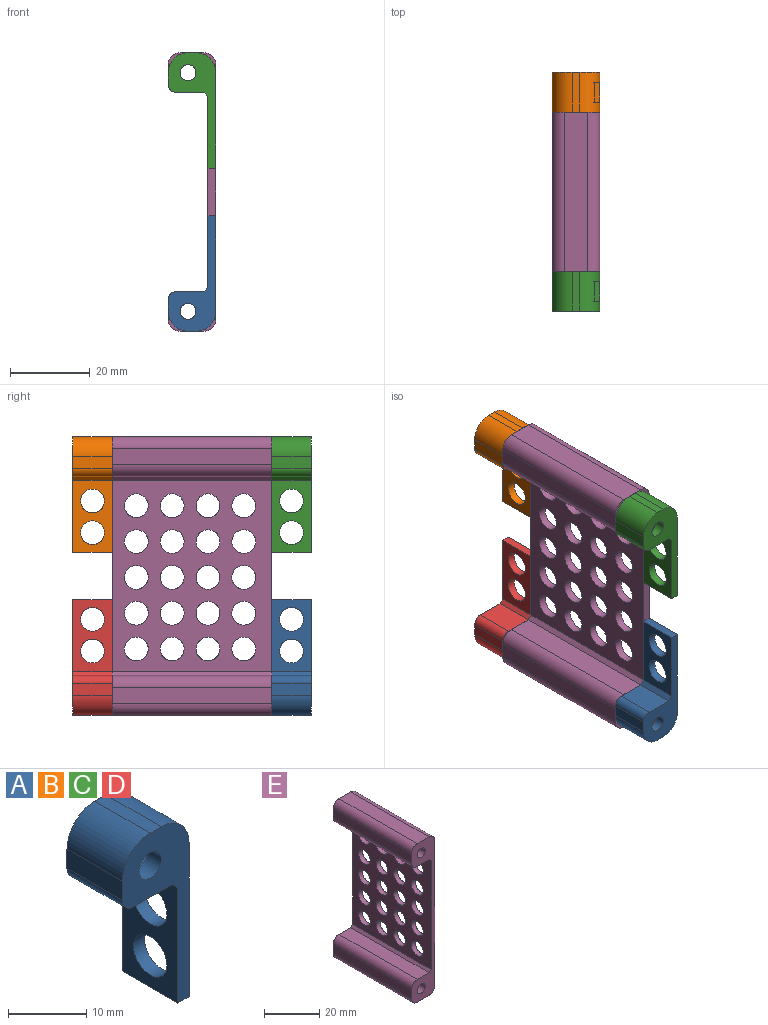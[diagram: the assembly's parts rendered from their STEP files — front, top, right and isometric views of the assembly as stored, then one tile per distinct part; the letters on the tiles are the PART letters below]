
ASSEMBLY  parts=5 mates=4
PART A: 22 faces, bbox 12x10x29 mm
  f0: plane 24x10mm, normal (1,0,0), area 165.9mm2, adj f1,f10,f11,f12,f17,f18,f19,f20
  f1: cylinder r=5mm len=10mm, axis (0,1,0), area 59.1mm2, adj f0,f3,f11,f12,f14,f18,f19
  f2: cylinder r=2mm len=4mm, axis (0,1,0), area 31.4mm2, adj f12,f18
  f3: plane 10x2mm, normal (0,0,1), area 20mm2, adj f1,f4,f11,f12
  f4: cylinder r=5mm len=10mm, axis (0,1,0), area 78.5mm2, adj f3,f5,f11,f12
  f5: plane 10x3mm, normal (-1,0,0), area 30mm2, adj f4,f6,f11,f12
  f6: cylinder r=2mm len=10mm, axis (0,1,0), area 31.4mm2, adj f5,f7,f11,f12
  f7: plane 10x7mm, normal (0,0,-1), area 70mm2, adj f6,f11,f12,f13
  f8: plane 18x10mm, normal (-1,0,0), area 123.5mm2, adj f10,f11,f12,f13,f20,f21
  f9: cylinder r=2mm len=4mm, axis (0,1,0), area 31.4mm2, adj f11,f19
  f10: plane 10x2mm, normal (0,0,-1), area 20mm2, adj f0,f8,f11,f12
  f11: plane 29x12mm, normal (0,-1,0), area 134.3mm2, adj f0,f1,f3,f4,f5,f6,f7,f8
  f12: plane 29x12mm, normal (0,1,0), area 134.3mm2, adj f0,f1,f2,f3,f4,f5,f6,f7
  f13: plane 10x1mm, normal (-0.71,0,-0.71), area 14.1mm2, adj f7,f8,f11,f12
  f14: plane 7.59x5mm, normal (0,0,-1), area 37.9mm2, adj f1,f15,f18,f19
  f15: plane 5x3.51mm, normal (0.87,0,-0.5), area 20.3mm2, adj f14,f16,f18,f19
  f16: plane 5x3.51mm, normal (0.87,0,0.5), area 20.3mm2, adj f15,f17,f18,f19
  f17: plane 9.03x5mm, normal (0,0,1), area 45.1mm2, adj f0,f16,f18,f19
  f18: plane 11.05x7.02mm, normal (0,-1,0), area 56.3mm2, adj f0,f1,f2,f14,f15,f16,f17
  f19: plane 11.05x7.02mm, normal (0,1,0), area 56.3mm2, adj f0,f1,f9,f14,f15,f16,f17
  f20: cylinder r=3mm len=6mm, axis (-1,0,0), area 37.7mm2, adj f0,f8
  f21: cylinder r=3mm len=6mm, axis (-1,0,0), area 37.7mm2, adj f0,f8
PART B: same geometry as A
PART C: same geometry as A
PART D: same geometry as A
PART E: 40 faces, bbox 12x40x70 mm
  f0: plane 48x40mm, normal (-1,0,0), area 1354.5mm2, adj f16,f17,f18,f19,f20,f21,f22,f23
  f1: plane 40x6mm, normal (0,0,1), area 240mm2, adj f2,f16,f17,f19
  f2: cylinder r=3mm len=40mm, axis (0,1,0), area 188.5mm2, adj f1,f3,f16,f17
  f3: plane 40x4mm, normal (-1,0,0), area 160mm2, adj f2,f4,f16,f17
  f4: cylinder r=3mm len=40mm, axis (0,1,0), area 188.5mm2, adj f3,f5,f16,f17
  f5: plane 40x6mm, normal (0,0,-1), area 240mm2, adj f4,f6,f16,f17
  f6: cylinder r=3mm len=40mm, axis (0,1,0), area 188.5mm2, adj f5,f7,f16,f17
  f7: plane 64x40mm, normal (1,0,0), area 1994.5mm2, adj f6,f8,f16,f17,f20,f21,f22,f23
  f8: cylinder r=3mm len=40mm, axis (0,1,0), area 188.5mm2, adj f7,f9,f16,f17
  f9: plane 40x6mm, normal (0,0,1), area 240mm2, adj f8,f10,f16,f17
  f10: cylinder r=3mm len=40mm, axis (0,1,0), area 188.5mm2, adj f9,f11,f16,f17
  f11: plane 40x4mm, normal (-1,0,0), area 160mm2, adj f10,f12,f16,f17
  f12: cylinder r=3mm len=40mm, axis (0,1,0), area 188.5mm2, adj f11,f14,f16,f17
  f13: cylinder r=2mm len=40mm, axis (0,1,0), area 502.7mm2, adj f16,f17
  f14: plane 40x6mm, normal (0,0,-1), area 240mm2, adj f12,f16,f17,f18
  f15: cylinder r=2mm len=40mm, axis (0,1,0), area 502.7mm2, adj f16,f17
  f16: plane 70x12mm, normal (0,-1,0), area 304.3mm2, adj f0,f1,f2,f3,f4,f5,f6,f7
  f17: plane 70x12mm, normal (0,1,0), area 304.3mm2, adj f0,f1,f2,f3,f4,f5,f6,f7
  f18: plane 40x1mm, normal (-0.71,0,-0.71), area 56.6mm2, adj f0,f14,f16,f17
  f19: plane 40x1mm, normal (-0.71,0,0.71), area 56.6mm2, adj f0,f1,f16,f17
  f20: cylinder r=3mm len=6mm, axis (-1,0,0), area 37.7mm2, adj f0,f7
  f21: cylinder r=3mm len=6mm, axis (-1,0,0), area 37.7mm2, adj f0,f7
  f22: cylinder r=3mm len=6mm, axis (-1,0,0), area 37.7mm2, adj f0,f7
  f23: cylinder r=3mm len=6mm, axis (-1,0,0), area 37.7mm2, adj f0,f7
  f24: cylinder r=3mm len=6mm, axis (-1,0,0), area 37.7mm2, adj f0,f7
  f25: cylinder r=3mm len=6mm, axis (-1,0,0), area 37.7mm2, adj f0,f7
  f26: cylinder r=3mm len=6mm, axis (-1,0,0), area 37.7mm2, adj f0,f7
  f27: cylinder r=3mm len=6mm, axis (-1,0,0), area 37.7mm2, adj f0,f7
  f28: cylinder r=3mm len=6mm, axis (-1,0,0), area 37.7mm2, adj f0,f7
  f29: cylinder r=3mm len=6mm, axis (-1,0,0), area 37.7mm2, adj f0,f7
  f30: cylinder r=3mm len=6mm, axis (-1,0,0), area 37.7mm2, adj f0,f7
  f31: cylinder r=3mm len=6mm, axis (-1,0,0), area 37.7mm2, adj f0,f7
  f32: cylinder r=3mm len=6mm, axis (-1,0,0), area 37.7mm2, adj f0,f7
  f33: cylinder r=3mm len=6mm, axis (-1,0,0), area 37.7mm2, adj f0,f7
  f34: cylinder r=3mm len=6mm, axis (-1,0,0), area 37.7mm2, adj f0,f7
  f35: cylinder r=3mm len=6mm, axis (-1,0,0), area 37.7mm2, adj f0,f7
  f36: cylinder r=3mm len=6mm, axis (-1,0,0), area 37.7mm2, adj f0,f7
  f37: cylinder r=3mm len=6mm, axis (-1,0,0), area 37.7mm2, adj f0,f7
  f38: cylinder r=3mm len=6mm, axis (-1,0,0), area 37.7mm2, adj f0,f7
  f39: cylinder r=3mm len=6mm, axis (-1,0,0), area 37.7mm2, adj f0,f7
PLACE A rot(axis=(1,0,0),180deg) t=(23.27,-24.29,-25.42)mm
PLACE B t=(23.27,25.71,-13.42)mm
PLACE C t=(23.27,-24.29,-13.42)mm
PLACE D rot(axis=(1,0,0),180deg) t=(23.27,25.71,-25.42)mm
PLACE E t=(23.27,20.71,-19.42)mm fixed
MATE fastened C.f2 <-> E.f13  axis (0,1,0) through (18.27,-19.29,10.58)mm
MATE fastened E.f13 <-> B.f2  axis (0,1,0) through (18.27,20.71,10.58)mm
MATE fastened E.f15 <-> D.f2  axis (0,1,0) through (18.27,20.71,-49.42)mm
MATE fastened E.f15 <-> A.f2  axis (0,-1,0) through (18.27,-19.29,-49.42)mm
